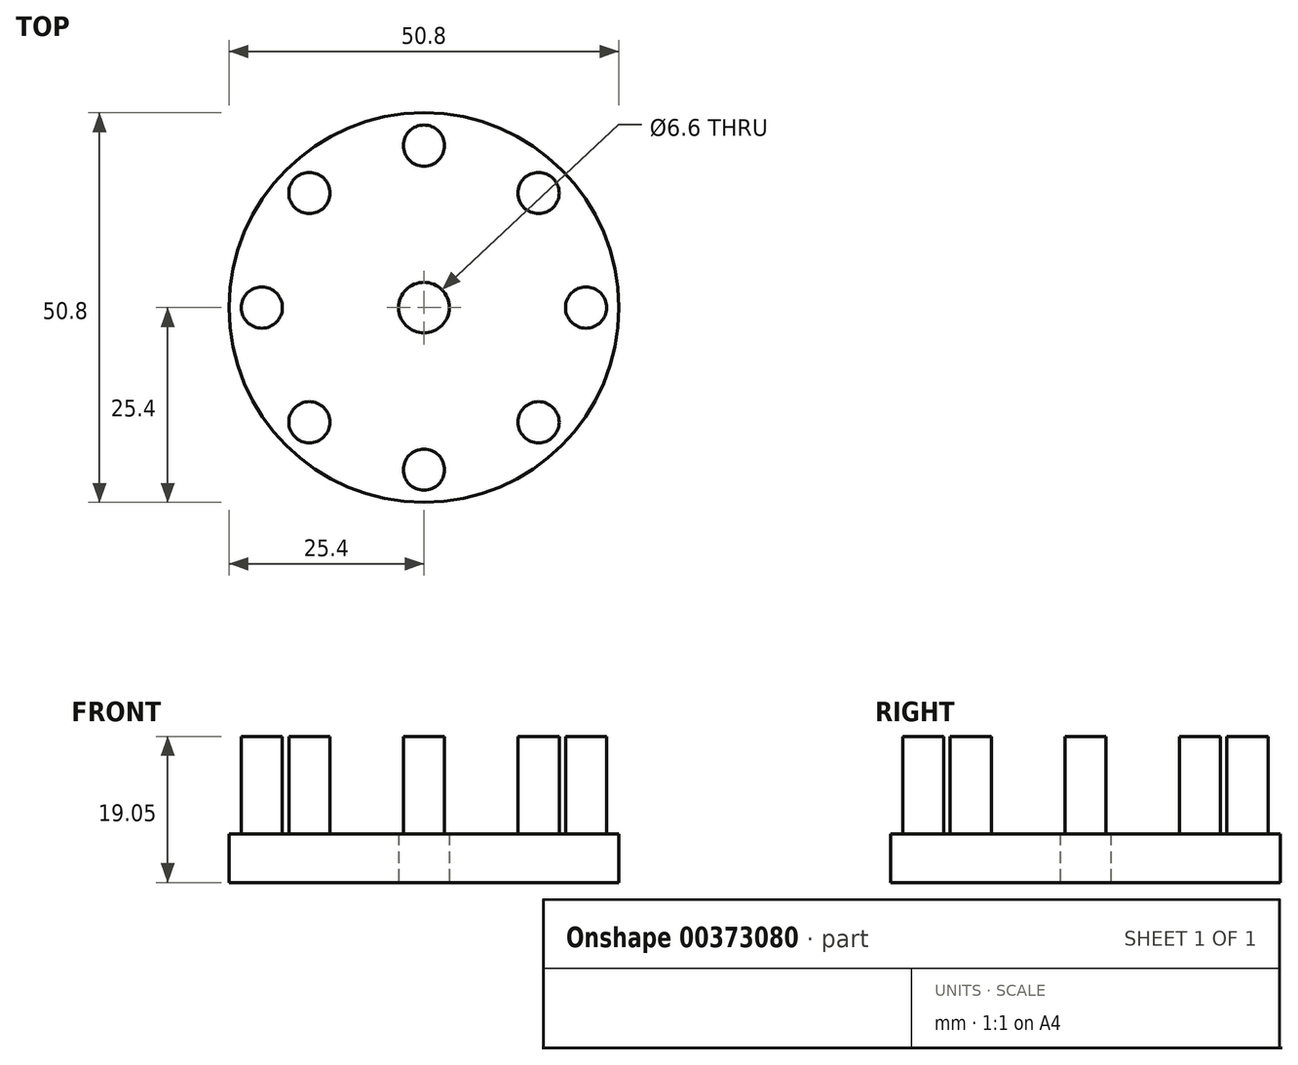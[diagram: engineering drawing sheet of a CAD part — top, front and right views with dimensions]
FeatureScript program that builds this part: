
annotation { "Feature Type Name" : "Feature", "Feature Type Description" : "" }
export const myFeature = defineFeature(function(context is Context, id is Id, definition is map)
    precondition{}
    {
        {
            var Q0;
            Q0=qCreatedBy(makeId("Top.planeOp"),FACE);
            var sketch = newSketch(context, id + "F0", { "sketchPlane" : qUnion([Q0])});
            skCircle(sketch, "E0", {"center": v(0, 0) * mm, "radius": 25.4 * mm});
            skCircle(sketch, "E1", {"center": v(0, 0) * mm, "radius": 3.3 * mm});
            skSolve(sketch);
        }
        {
            var Q0;
            Q0 = qSketchRegion(id + "F0", true);
            extrude(context, id + "F1", {"entities" : qUnion([Q0]), "depth" : 6.35 * mm});
        }
        {
            var Q0;
            Q0=makeQuery(id+"F1.opExtrude","CAP_FACE",FACE,{"disambiguationData":[OSD([sQuery(id+"F0.wireOp",EDGE,"E0"),sQuery(id+"F0.wireOp",EDGE,"E1")])],"isStart":false});
            var sketch = newSketch(context, id + "F2", { "sketchPlane" : qUnion([Q0])});
            skCircle(sketch, "E2", {"center": v(0, 21.13) * mm, "radius": 2.68 * mm});
            skCircle(sketch, "E3.1.0", {"center": v(-14.94, 14.94) * mm, "radius": 2.68 * mm});
            skCircle(sketch, "E3.2.0", {"center": v(-21.13, 0) * mm, "radius": 2.68 * mm});
            skCircle(sketch, "E3.3.0", {"center": v(-14.94, -14.94) * mm, "radius": 2.68 * mm});
            skCircle(sketch, "E3.4.0", {"center": v(0, -21.13) * mm, "radius": 2.68 * mm});
            skCircle(sketch, "E3.5.0", {"center": v(14.94, -14.94) * mm, "radius": 2.68 * mm});
            skCircle(sketch, "E3.6.0", {"center": v(21.13, 0) * mm, "radius": 2.68 * mm});
            skCircle(sketch, "E3.7.0", {"center": v(14.94, 14.94) * mm, "radius": 2.68 * mm});
            skPoint(sketch, "E3.center", {"position": v(0, 0) * mm});
            skSolve(sketch);
        }
        {
            var Q0;
            Q0=makeQuery(id+"F2.imprint","IMPRINT",FACE,{"disambiguationData":[TD([[makeQuery(id+"F2.imprint","IMPRINT",EDGE,{"derivedFrom":sQuery(id+"F2.wireOp",EDGE,"E2")}),1.0]])]});
            var Q1;
            Q1=makeQuery(id+"F2.imprint","IMPRINT",FACE,{"disambiguationData":[TD([[makeQuery(id+"F2.imprint","IMPRINT",EDGE,{"derivedFrom":sQuery(id+"F2.wireOp",EDGE,"E3.1.0")}),1.0]])]});
            var Q2;
            Q2=makeQuery(id+"F2.imprint","IMPRINT",FACE,{"disambiguationData":[TD([[makeQuery(id+"F2.imprint","IMPRINT",EDGE,{"derivedFrom":sQuery(id+"F2.wireOp",EDGE,"E3.2.0")}),1.0]])]});
            var Q3;
            Q3=makeQuery(id+"F2.imprint","IMPRINT",FACE,{"disambiguationData":[TD([[makeQuery(id+"F2.imprint","IMPRINT",EDGE,{"derivedFrom":sQuery(id+"F2.wireOp",EDGE,"E3.3.0")}),1.0]])]});
            var Q4;
            Q4=makeQuery(id+"F2.imprint","IMPRINT",FACE,{"disambiguationData":[TD([[makeQuery(id+"F2.imprint","IMPRINT",EDGE,{"derivedFrom":sQuery(id+"F2.wireOp",EDGE,"E3.4.0")}),1.0]])]});
            var Q5;
            Q5=makeQuery(id+"F2.imprint","IMPRINT",FACE,{"disambiguationData":[TD([[makeQuery(id+"F2.imprint","IMPRINT",EDGE,{"derivedFrom":sQuery(id+"F2.wireOp",EDGE,"E3.6.0")}),1.0]])]});
            var Q6;
            Q6=makeQuery(id+"F2.imprint","IMPRINT",FACE,{"disambiguationData":[TD([[makeQuery(id+"F2.imprint","IMPRINT",EDGE,{"derivedFrom":sQuery(id+"F2.wireOp",EDGE,"E3.7.0")}),1.0]])]});
            var Q7;
            Q7=makeQuery(id+"F2.imprint","IMPRINT",FACE,{"disambiguationData":[TD([[makeQuery(id+"F2.imprint","IMPRINT",EDGE,{"derivedFrom":sQuery(id+"F2.wireOp",EDGE,"E3.5.0")}),1.0]])]});
            var Q8;
            Q8=sQuery(id+"F2.wireOp",EDGE,"E3.1.0");
            var Q9;
            Q9=sQuery(id+"F2.wireOp",EDGE,"E2");
            var Q10;
            Q10=sQuery(id+"F2.wireOp",EDGE,"E3.7.0");
            extrude(context, id + "F3", {"entities" : qUnion([Q0, Q1, Q2, Q3, Q4, Q5, Q6, Q7]), "operationType" : NewBodyOperationType.ADD, "surfaceEntities" : qUnion([Q8, Q9, Q10]), "depth" : 12.7 * mm});
        }
    });
